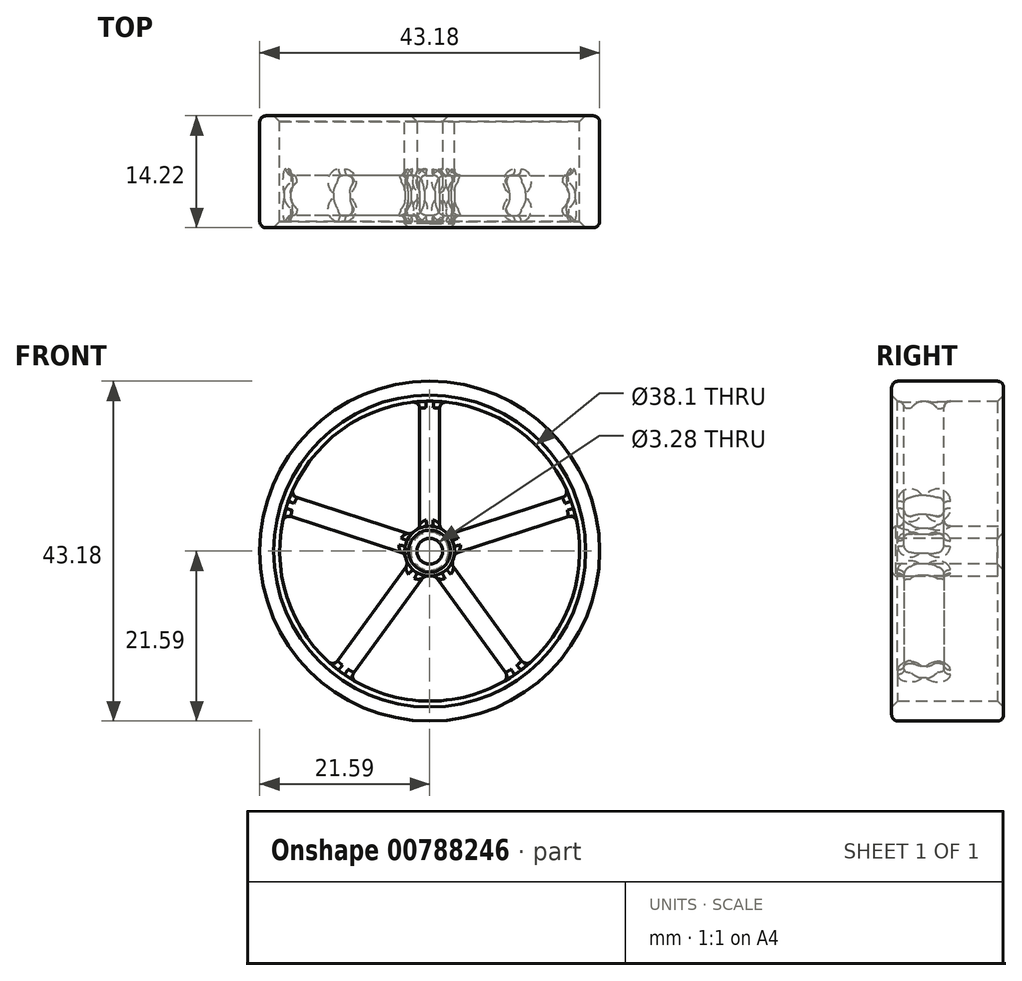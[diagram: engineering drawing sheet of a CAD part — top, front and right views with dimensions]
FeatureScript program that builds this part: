
annotation { "Feature Type Name" : "Feature", "Feature Type Description" : "" }
export const myFeature = defineFeature(function(context is Context, id is Id, definition is map)
    precondition{}
    {
        {
            var Q0;
            Q0=qCreatedBy(makeId("Top.planeOp"),FACE);
            var sketch = newSketch(context, id + "F0", { "sketchPlane" : qUnion([Q0])});
            skLineSegment(sketch, "E0", {"start": v(0, 0) * mm, "end": v(-3.18, 0) * mm});
            skLineSegment(sketch, "E1", {"start": v(-3.18, 0) * mm, "end": v(-3.17, -7.57) * mm});
            skLineSegment(sketch, "E2", {"start": v(-3.17, -7.57) * mm, "end": v(-19.05, -7.57) * mm});
            skLineSegment(sketch, "E3", {"start": v(-19.05, -7.57) * mm, "end": v(-19.05, 0) * mm});
            skLineSegment(sketch, "E4", {"start": v(-19.05, 0) * mm, "end": v(-21.59, 0) * mm});
            skLineSegment(sketch, "E5", {"start": v(-21.59, 0) * mm, "end": v(-21.59, -14.22) * mm});
            skLineSegment(sketch, "E6", {"start": v(0, -14.22) * mm, "end": v(0, 0) * mm});
            skLineSegment(sketch, "E7", {"start": v(0, 19.15) * mm, "end": v(0, -30.68) * mm, "construction": true});
            skLineSegment(sketch, "E8", {"start": v(-21.59, -14.22) * mm, "end": v(-19.05, -14.22) * mm});
            skLineSegment(sketch, "E9", {"start": v(-19.05, -14.22) * mm, "end": v(-19.05, -12.65) * mm});
            skLineSegment(sketch, "E10", {"start": v(-19.05, -12.65) * mm, "end": v(-3.17, -12.65) * mm});
            skLineSegment(sketch, "E11", {"start": v(-3.18, -12.65) * mm, "end": v(-3.18, -14.22) * mm});
            skLineSegment(sketch, "E12", {"start": v(-3.18, -14.22) * mm, "end": v(0, -14.22) * mm});
            skSolve(sketch);
        }
        {
            var Q0;
            Q0=makeQuery(id+"F0.imprint","IMPRINT",FACE,{"disambiguationData":[TD([[makeQuery(id+"F0.imprint","IMPRINT",EDGE,{"derivedFrom":sQuery(id+"F0.wireOp",EDGE,"E0")}),1.0]])]});
            var Q1;
            Q1=sQuery(id+"F0.wireOp",EDGE,"E7");
            revolve(context, id + "F1", {"surfaceOperationType" : NewSurfaceOperationType.NEW, "entities" : qUnion([Q0]), "axis" : qUnion([Q1]), "revolveType" : RevolveType.FULL});
        }
        {
            var Q0;
            Q0=makeQuery(id+"F1.opRevolve","SWEPT_FACE",FACE,{"disambiguationData":[OSD([sQuery(id+"F0.wireOp",EDGE,"E10")])]});
            var sketch = newSketch(context, id + "F2", { "sketchPlane" : qUnion([Q0])});
            skPoint(sketch, "E13.orphan", {"position": v(0, 0) * mm});
            skLineSegment(sketch, "E14.right", {"start": v(1.27, 2.9) * mm, "end": v(1.27, 19) * mm});
            skLineSegment(sketch, "E15.MirrorCS", {"start": v(-1.27, 2.9) * mm, "end": v(-1.27, 19) * mm});
            skArc(sketch, "E16.0", {"start": v(1.27, 2.9) * mm, "mid": v(0, 3.17) * mm, "end": v(-1.27, 2.9) * mm});
            skPoint(sketch, "E17.orphan", {"position": v(-1.27, 0) * mm});
            skPoint(sketch, "E18.orphan", {"position": v(1.27, 0) * mm});
            skPoint(sketch, "E19.MirrorCS.end.orphan", {"position": v(-1.27, 20.32) * mm});
            skPoint(sketch, "E19.MirrorCS.start.orphan", {"position": v(0, 20.32) * mm});
            skArc(sketch, "E20.0", {"start": v(1.27, 19) * mm, "mid": v(0, 19.05) * mm, "end": v(-1.27, 19) * mm});
            skPoint(sketch, "E21.orphan", {"position": v(1.27, 20.32) * mm});
            skLineSegment(sketch, "E22.1.0", {"start": v(-2.38, 2.1) * mm, "end": v(-17.68, 7.08) * mm});
            skLineSegment(sketch, "E22.1.1", {"start": v(-3.16, -0.3) * mm, "end": v(-18.47, 4.67) * mm});
            skLineSegment(sketch, "E22.2.0", {"start": v(-2.74, -1.6) * mm, "end": v(-12.2, -14.63) * mm});
            skLineSegment(sketch, "E22.2.1", {"start": v(-0.68, -3.1) * mm, "end": v(-10.14, -16.12) * mm});
            skLineSegment(sketch, "E22.3.0", {"start": v(0.68, -3.1) * mm, "end": v(10.14, -16.12) * mm});
            skLineSegment(sketch, "E22.3.1", {"start": v(2.74, -1.6) * mm, "end": v(12.2, -14.63) * mm});
            skLineSegment(sketch, "E22.4.0", {"start": v(3.16, -0.3) * mm, "end": v(18.47, 4.67) * mm});
            skLineSegment(sketch, "E22.4.1", {"start": v(2.38, 2.1) * mm, "end": v(17.68, 7.08) * mm});
            skSolve(sketch);
        }
        {
            var Q0;
            {var subQ0=sQuery(id+"F2.wireOp",EDGE,"E15.MirrorCS");Q0=makeQuery(id+"F2.imprint","IMPRINT",FACE,{"disambiguationData":[TD([[makeQuery(id+"F2.imprint","IMPRINT",EDGE,{"derivedFrom":subQ0}),1.0]])]});}
            var Q1;
            {var subQ0=sQuery(id+"F2.wireOp",EDGE,"E22.1.1");Q1=makeQuery(id+"F2.imprint","IMPRINT",FACE,{"disambiguationData":[TD([[makeQuery(id+"F2.imprint","IMPRINT",EDGE,{"derivedFrom":subQ0}),1.0]])]});}
            var Q2;
            {var subQ0=sQuery(id+"F2.wireOp",EDGE,"E22.2.1");Q2=makeQuery(id+"F2.imprint","IMPRINT",FACE,{"disambiguationData":[TD([[makeQuery(id+"F2.imprint","IMPRINT",EDGE,{"derivedFrom":subQ0}),1.0]])]});}
            var Q3;
            {var subQ0=sQuery(id+"F2.wireOp",EDGE,"E22.3.1");Q3=makeQuery(id+"F2.imprint","IMPRINT",FACE,{"disambiguationData":[TD([[makeQuery(id+"F2.imprint","IMPRINT",EDGE,{"derivedFrom":subQ0}),1.0]])]});}
            var Q4;
            {var subQ0=sQuery(id+"F2.wireOp",EDGE,"E14.right");Q4=makeQuery(id+"F2.imprint","IMPRINT",FACE,{"disambiguationData":[TD([[makeQuery(id+"F2.imprint","IMPRINT",EDGE,{"derivedFrom":subQ0}),-1.0]])]});}
            extrude(context, id + "F3", {"entities" : qUnion([Q0, Q1, Q2, Q3, Q4]), "operationType" : NewBodyOperationType.REMOVE, "endBound" : BoundingType.UP_TO_NEXT, "oppositeDirection" : true, "depth" : 25.4 * mm, "offsetDistance" : 25.4 * mm});
        }
        {
            var Q0;
            Q0=makeQuery(id+"F1.opRevolve","SWEPT_FACE",FACE,{"disambiguationData":[OSD([sQuery(id+"F0.wireOp",EDGE,"E12")])]});
            var sketch = newSketch(context, id + "F4", { "sketchPlane" : qUnion([Q0])});
            skCircle(sketch, "E23", {"center": v(0, 0) * mm, "radius": 1.64 * mm});
            skSolve(sketch);
        }
        {
            var Q0;
            Q0 = qSketchRegion(id + "F4", true);
            extrude(context, id + "F5", {"entities" : qUnion([Q0]), "operationType" : NewBodyOperationType.REMOVE, "endBound" : BoundingType.THROUGH_ALL, "oppositeDirection" : true, "depth" : 25.4 * mm, "offsetDistance" : 25.4 * mm});
        }
        {
            var Q0;
            {var subQ1=sQuery(id+"F0.wireOp",EDGE,"E10");var subQ7=sQuery(id+"F2.wireOp",EDGE,"E22.1.0");Q0=makeQuery(id+"F3.boolean.opBoolean","SPLIT",FACE,{"disambiguationData":[TD([makeQuery(id+"F3.opExtrude","SWEPT_FACE",FACE,{"disambiguationData":[OSD([subQ7])]})])],"derivedFrom":makeQuery(id+"F1.opRevolve","SWEPT_FACE",FACE,{"disambiguationData":[OSD([subQ1])]})});}
            var Q1;
            {var subQ1=sQuery(id+"F0.wireOp",EDGE,"E10");var subQ8=sQuery(id+"F2.wireOp",EDGE,"E14.right");Q1=makeQuery(id+"F3.boolean.opBoolean","SPLIT",FACE,{"disambiguationData":[TD([makeQuery(id+"F3.opExtrude","SWEPT_FACE",FACE,{"disambiguationData":[OSD([subQ8])]})])],"derivedFrom":makeQuery(id+"F1.opRevolve","SWEPT_FACE",FACE,{"disambiguationData":[OSD([subQ1])]})});}
            var Q2;
            {var subQ1=sQuery(id+"F0.wireOp",EDGE,"E10");var subQ13=sQuery(id+"F2.wireOp",EDGE,"E22.4.0");Q2=makeQuery(id+"F3.boolean.opBoolean","SPLIT",FACE,{"disambiguationData":[TD([makeQuery(id+"F3.opExtrude","SWEPT_FACE",FACE,{"disambiguationData":[OSD([subQ13])]})])],"derivedFrom":makeQuery(id+"F1.opRevolve","SWEPT_FACE",FACE,{"disambiguationData":[OSD([subQ1])]})});}
            var Q3;
            {var subQ1=sQuery(id+"F0.wireOp",EDGE,"E10");var subQ4=sQuery(id+"F2.wireOp",EDGE,"E22.3.0");Q3=makeQuery(id+"F3.boolean.opBoolean","SPLIT",FACE,{"disambiguationData":[TD([makeQuery(id+"F3.opExtrude","SWEPT_FACE",FACE,{"disambiguationData":[OSD([subQ4])]})])],"derivedFrom":makeQuery(id+"F1.opRevolve","SWEPT_FACE",FACE,{"disambiguationData":[OSD([subQ1])]})});}
            var Q4;
            {var subQ2=sQuery(id+"F0.wireOp",EDGE,"E10");var subQ10=sQuery(id+"F2.wireOp",EDGE,"E22.2.0");Q4=makeQuery(id+"F3.boolean.opBoolean","SPLIT",FACE,{"disambiguationData":[TD([makeQuery(id+"F3.opExtrude","SWEPT_FACE",FACE,{"disambiguationData":[OSD([subQ10])]})])],"derivedFrom":makeQuery(id+"F1.opRevolve","SWEPT_FACE",FACE,{"disambiguationData":[OSD([subQ2])]})});}
            var Q5;
            {var subQ7=sQuery(id+"F2.wireOp",EDGE,"E22.1.0");Q5=makeQuery(id+"F3.boolean.opBoolean","SPLIT",FACE,{"disambiguationData":[TD([makeQuery(id+"F3.opExtrude","SWEPT_FACE",FACE,{"disambiguationData":[OSD([subQ7])]})])],"derivedFrom":makeQuery(id+"F1.opRevolve","SWEPT_FACE",FACE,{"disambiguationData":[OSD([sQuery(id+"F0.wireOp",EDGE,"E2")])]})});}
            var Q6;
            {var subQ8=sQuery(id+"F2.wireOp",EDGE,"E14.right");Q6=makeQuery(id+"F3.boolean.opBoolean","SPLIT",FACE,{"disambiguationData":[TD([makeQuery(id+"F3.opExtrude","SWEPT_FACE",FACE,{"disambiguationData":[OSD([subQ8])]})])],"derivedFrom":makeQuery(id+"F1.opRevolve","SWEPT_FACE",FACE,{"disambiguationData":[OSD([sQuery(id+"F0.wireOp",EDGE,"E2")])]})});}
            var Q7;
            {var subQ13=sQuery(id+"F2.wireOp",EDGE,"E22.4.0");Q7=makeQuery(id+"F3.boolean.opBoolean","SPLIT",FACE,{"disambiguationData":[TD([makeQuery(id+"F3.opExtrude","SWEPT_FACE",FACE,{"disambiguationData":[OSD([subQ13])]})])],"derivedFrom":makeQuery(id+"F1.opRevolve","SWEPT_FACE",FACE,{"disambiguationData":[OSD([sQuery(id+"F0.wireOp",EDGE,"E2")])]})});}
            var Q8;
            {var subQ4=sQuery(id+"F2.wireOp",EDGE,"E22.3.0");Q8=makeQuery(id+"F3.boolean.opBoolean","SPLIT",FACE,{"disambiguationData":[TD([makeQuery(id+"F3.opExtrude","SWEPT_FACE",FACE,{"disambiguationData":[OSD([subQ4])]})])],"derivedFrom":makeQuery(id+"F1.opRevolve","SWEPT_FACE",FACE,{"disambiguationData":[OSD([sQuery(id+"F0.wireOp",EDGE,"E2")])]})});}
            var Q9;
            {var subQ10=sQuery(id+"F2.wireOp",EDGE,"E22.2.0");Q9=makeQuery(id+"F3.boolean.opBoolean","SPLIT",FACE,{"disambiguationData":[TD([makeQuery(id+"F3.opExtrude","SWEPT_FACE",FACE,{"disambiguationData":[OSD([subQ10])]})])],"derivedFrom":makeQuery(id+"F1.opRevolve","SWEPT_FACE",FACE,{"disambiguationData":[OSD([sQuery(id+"F0.wireOp",EDGE,"E2")])]})});}
            var Q10;
            Q10=makeQuery(id+"F1.opRevolve","SWEPT_EDGE",EDGE,{"disambiguationData":[OSD([sQuery(id+"F0.wireOp",EDGE,"E5"),sQuery(id+"F0.wireOp",EDGE,"E8")])]});
            var Q11;
            Q11=makeQuery(id+"F1.opRevolve","SWEPT_EDGE",EDGE,{"disambiguationData":[OSD([sQuery(id+"F0.wireOp",EDGE,"E4"),sQuery(id+"F0.wireOp",EDGE,"E5")])]});
            fillet(context, id + "F6", {"entities" : qUnion([Q0, Q1, Q2, Q3, Q4, Q5, Q6, Q7, Q8, Q9, Q10, Q11]), "radius" : 0.81 * mm, "tangentPropagation" : true, "allowEdgeOverflow" : false});
        }
        {
            var Q0;
            Q0=makeQuery(id+"F5.boolean.opBoolean","INTERSECT",EDGE,{"derivedFrom":[makeQuery(id+"F1.opRevolve","SWEPT_FACE",FACE,{"disambiguationData":[OSD([sQuery(id+"F0.wireOp",EDGE,"E0")])]}),makeQuery(id+"F5.opExtrude","SWEPT_FACE",FACE,{"disambiguationData":[OSD([sQuery(id+"F4.wireOp",EDGE,"E23")])]})]});
            var Q1;
            Q1=makeQuery(id+"F1.opRevolve","SWEPT_EDGE",EDGE,{"disambiguationData":[OSD([sQuery(id+"F0.wireOp",EDGE,"E3"),sQuery(id+"F0.wireOp",EDGE,"E4")])]});
            var Q2;
            Q2=makeQuery(id+"F1.opRevolve","SWEPT_EDGE",EDGE,{"disambiguationData":[OSD([sQuery(id+"F0.wireOp",EDGE,"E8"),sQuery(id+"F0.wireOp",EDGE,"E9")])]});
            chamfer(context, id + "F7", {"entities" : qUnion([Q0, Q1, Q2]), "width" : 0.76 * mm, "tangentPropagation" : true});
        }
        {
            var Q0;
            Q0=makeQuery(id+"F1.opRevolve","SWEPT_EDGE",EDGE,{"disambiguationData":[OSD([sQuery(id+"F0.wireOp",EDGE,"E11"),sQuery(id+"F0.wireOp",EDGE,"E12")])]});
            chamfer(context, id + "F8", {"entities" : qUnion([Q0]), "width" : 0.5 * mm, "tangentPropagation" : true});
        }
    });
